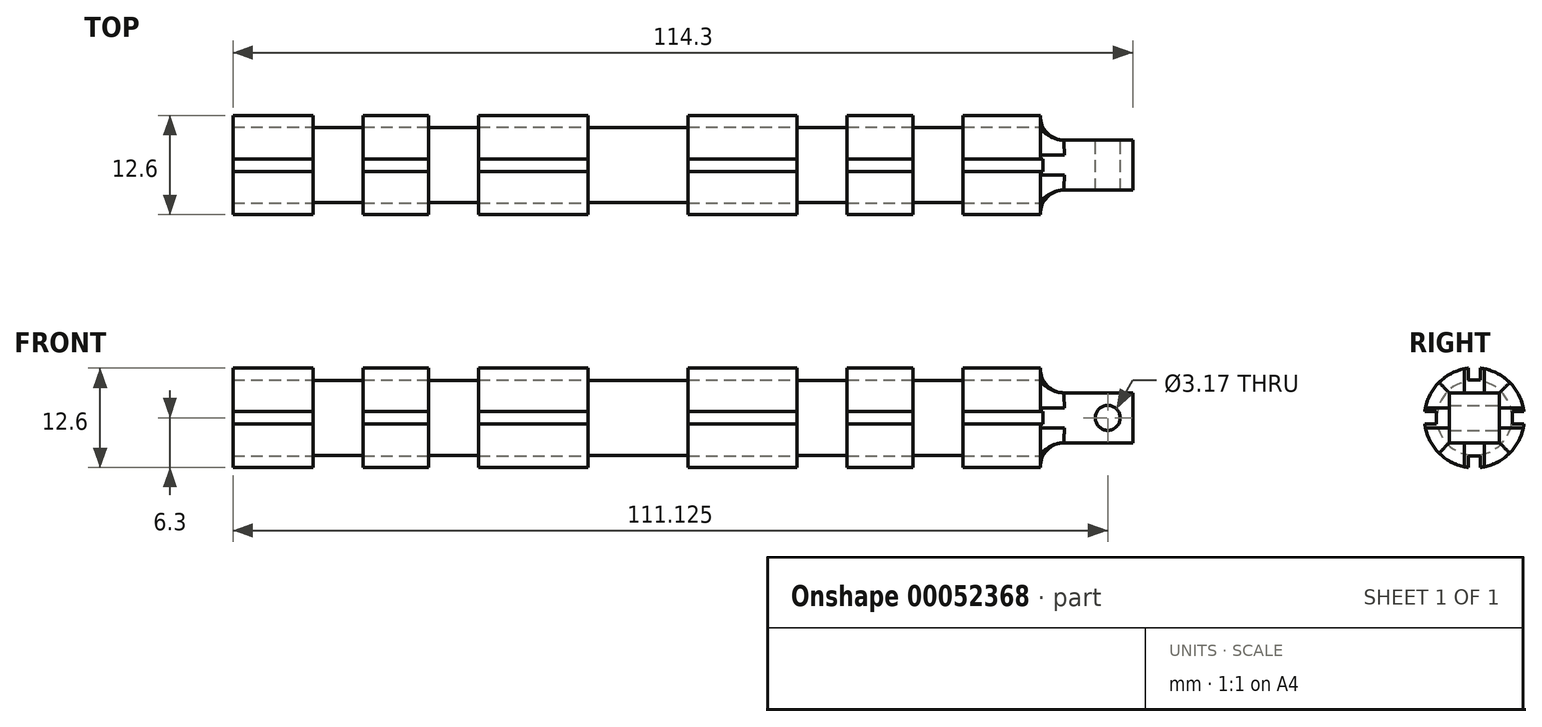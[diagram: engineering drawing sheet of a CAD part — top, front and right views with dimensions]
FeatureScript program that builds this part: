
annotation { "Feature Type Name" : "Feature", "Feature Type Description" : "" }
export const myFeature = defineFeature(function(context is Context, id is Id, definition is map)
    precondition{}
    {
        {
            var Q0;
            Q0=qCreatedBy(makeId("Front.planeOp"),FACE);
            var sketch = newSketch(context, id + "F0", { "sketchPlane" : qUnion([Q0])});
            skLineSegment(sketch, "E0", {"start": v(-57.15, 0) * mm, "end": v(57.15, 0) * mm});
            skLineSegment(sketch, "E1", {"start": v(57.15, 0) * mm, "end": v(57.15, 4.76) * mm});
            skLineSegment(sketch, "E2", {"start": v(45.4, 6.35) * mm, "end": v(35.56, 6.35) * mm});
            skLineSegment(sketch, "E3", {"start": v(35.56, 6.35) * mm, "end": v(35.56, 4.76) * mm});
            skLineSegment(sketch, "E4", {"start": v(35.56, 4.76) * mm, "end": v(29.21, 4.76) * mm});
            skLineSegment(sketch, "E5", {"start": v(29.21, 4.76) * mm, "end": v(29.21, 6.35) * mm});
            skLineSegment(sketch, "E6", {"start": v(29.21, 6.35) * mm, "end": v(20.88, 6.35) * mm});
            skLineSegment(sketch, "E7", {"start": v(20.88, 6.35) * mm, "end": v(20.88, 4.76) * mm});
            skLineSegment(sketch, "E8", {"start": v(20.88, 4.76) * mm, "end": v(14.53, 4.76) * mm});
            skLineSegment(sketch, "E9", {"start": v(14.53, 4.76) * mm, "end": v(14.53, 6.35) * mm});
            skLineSegment(sketch, "E10", {"start": v(14.53, 6.35) * mm, "end": v(0.63, 6.35) * mm});
            skLineSegment(sketch, "E11", {"start": v(0.63, 6.35) * mm, "end": v(0.63, 4.76) * mm});
            skLineSegment(sketch, "E12", {"start": v(0.63, 4.76) * mm, "end": v(-12.07, 4.76) * mm});
            skLineSegment(sketch, "E13", {"start": v(-12.07, 4.76) * mm, "end": v(-12.07, 6.35) * mm});
            skLineSegment(sketch, "E14", {"start": v(-12.07, 6.35) * mm, "end": v(-25.96, 6.35) * mm});
            skLineSegment(sketch, "E15", {"start": v(-25.96, 6.35) * mm, "end": v(-25.96, 4.76) * mm});
            skLineSegment(sketch, "E16", {"start": v(-25.96, 4.76) * mm, "end": v(-32.3, 4.76) * mm});
            skLineSegment(sketch, "E17", {"start": v(-32.3, 4.76) * mm, "end": v(-32.3, 6.35) * mm});
            skLineSegment(sketch, "E18", {"start": v(-32.3, 6.35) * mm, "end": v(-40.64, 6.35) * mm});
            skLineSegment(sketch, "E19", {"start": v(-40.64, 6.35) * mm, "end": v(-40.64, 4.76) * mm});
            skLineSegment(sketch, "E20", {"start": v(-40.64, 4.76) * mm, "end": v(-47, 4.76) * mm});
            skLineSegment(sketch, "E21", {"start": v(-47, 4.76) * mm, "end": v(-47, 6.35) * mm});
            skLineSegment(sketch, "E22", {"start": v(-47, 6.35) * mm, "end": v(-57.15, 6.35) * mm});
            skLineSegment(sketch, "E23", {"start": v(-57.15, 6.35) * mm, "end": v(-57.15, 0) * mm});
            skLineSegment(sketch, "E24", {"start": v(45.4, 6.35) * mm, "end": v(45.4, 4.76) * mm});
            skLineSegment(sketch, "E25", {"start": v(57.15, 4.76) * mm, "end": v(45.4, 4.76) * mm});
            skSolve(sketch);
        }
        {
            var Q0;
            Q0 = qSketchRegion(id + "F0", true);
            var Q1;
            Q1=sQuery(id+"F0.wireOp",EDGE,"E0");
            revolve(context, id + "F1", {"entities" : qUnion([Q0]), "axis" : qUnion([Q1]), "revolveType" : RevolveType.FULL});
        }
        {
            var Q0;
            Q0=makeQuery(id+"F1.opRevolve","SWEPT_FACE",FACE,{"disambiguationData":[OSD([sQuery(id+"F0.wireOp",EDGE,"E1")])]});
            var sketch = newSketch(context, id + "F2", { "sketchPlane" : qUnion([Q0])});
            skCircle(sketch, "E26.0", {"center": v(0, 0) * mm, "radius": 4.76 * mm});
            skLineSegment(sketch, "E27.rect.bottom", {"start": v(-3.17, 3.18) * mm, "end": v(3.18, 3.18) * mm});
            skLineSegment(sketch, "E27.rect.top", {"start": v(-3.18, -3.18) * mm, "end": v(3.17, -3.18) * mm});
            skLineSegment(sketch, "E27.rect.left", {"start": v(-3.17, 3.18) * mm, "end": v(-3.18, -3.17) * mm});
            skLineSegment(sketch, "E27.rect.right", {"start": v(3.18, 3.18) * mm, "end": v(3.17, -3.18) * mm});
            skSolve(sketch);
        }
        {
            var Q0;
            Q0 = qSketchRegion(id + "F2", true);
            extrude(context, id + "F3", {"entities" : qUnion([Q0]), "operationType" : NewBodyOperationType.REMOVE, "oppositeDirection" : true, "depth" : 11.75 * mm});
        }
        {
            var Q0;
            Q0=makeQuery(id+"F3.boolean.opBoolean","COPY",FACE,{"derivedFrom":makeQuery(id+"F3.opExtrude","SWEPT_FACE",FACE,{"disambiguationData":[OSD([sQuery(id+"F2.wireOp",EDGE,"E27.rect.left")])]})});
            var sketch = newSketch(context, id + "F4", { "sketchPlane" : qUnion([Q0])});
            skPoint(sketch, "E28", {"position": v(53.98, 0) * mm});
            skSolve(sketch);
        }
        {
            var Q0;
            Q0=sQuery(id+"F4.wireOp",VERTEX,"E28");
            var Q1;
            Q1=makeQuery(id+"F1.opRevolve","SWEPT_BODY",BODY,{"disambiguationData":[OSD([sQuery(id+"F0.wireOp",EDGE,"E0"),sQuery(id+"F0.wireOp",EDGE,"E1"),sQuery(id+"F0.wireOp",EDGE,"E2"),sQuery(id+"F0.wireOp",EDGE,"E3"),sQuery(id+"F0.wireOp",EDGE,"E4"),sQuery(id+"F0.wireOp",EDGE,"E5"),sQuery(id+"F0.wireOp",EDGE,"E6"),sQuery(id+"F0.wireOp",EDGE,"E7"),sQuery(id+"F0.wireOp",EDGE,"E8"),sQuery(id+"F0.wireOp",EDGE,"E9"),sQuery(id+"F0.wireOp",EDGE,"E10"),sQuery(id+"F0.wireOp",EDGE,"E11"),sQuery(id+"F0.wireOp",EDGE,"E12"),sQuery(id+"F0.wireOp",EDGE,"E13"),sQuery(id+"F0.wireOp",EDGE,"E14"),sQuery(id+"F0.wireOp",EDGE,"E15"),sQuery(id+"F0.wireOp",EDGE,"E16"),sQuery(id+"F0.wireOp",EDGE,"E17"),sQuery(id+"F0.wireOp",EDGE,"E18"),sQuery(id+"F0.wireOp",EDGE,"E19"),sQuery(id+"F0.wireOp",EDGE,"E20"),sQuery(id+"F0.wireOp",EDGE,"E21"),sQuery(id+"F0.wireOp",EDGE,"E22"),sQuery(id+"F0.wireOp",EDGE,"E23"),sQuery(id+"F0.wireOp",EDGE,"E24"),sQuery(id+"F0.wireOp",EDGE,"E25")])]});
            hole(context, id + "F5", {"style" : HoleStyle.SIMPLE, "holeDiameter" : 3.17 * mm, "endStyle" : HoleEndStyle.THROUGH, "locations" : qUnion([Q0]), "scope" : qUnion([Q1])});
        }
        {
            var Q0;
            Q0=makeQuery(id+"F3.boolean.opBoolean","COPY",EDGE,{"derivedFrom":makeQuery(id+"F3.opExtrude","CAP_EDGE",EDGE,{"disambiguationData":[OSD([sQuery(id+"F2.wireOp",EDGE,"E27.rect.bottom")])],"isStart":false})});
            var Q1;
            Q1=makeQuery(id+"F3.boolean.opBoolean","COPY",EDGE,{"derivedFrom":makeQuery(id+"F3.opExtrude","CAP_EDGE",EDGE,{"disambiguationData":[OSD([sQuery(id+"F2.wireOp",EDGE,"E27.rect.left")])],"isStart":false})});
            var Q2;
            Q2=makeQuery(id+"F3.boolean.opBoolean","COPY",EDGE,{"derivedFrom":makeQuery(id+"F3.opExtrude","CAP_EDGE",EDGE,{"disambiguationData":[OSD([sQuery(id+"F2.wireOp",EDGE,"E27.rect.top")])],"isStart":false})});
            var Q3;
            Q3=makeQuery(id+"F3.boolean.opBoolean","COPY",EDGE,{"derivedFrom":makeQuery(id+"F3.opExtrude","CAP_EDGE",EDGE,{"disambiguationData":[OSD([sQuery(id+"F2.wireOp",EDGE,"E27.rect.right")])],"isStart":false})});
            fillet(context, id + "F6", {"entities" : qUnion([Q0, Q1, Q2, Q3]), "radius" : 3.05 * mm, "tangentPropagation" : true, "allowEdgeOverflow" : false});
        }
        {
            var Q0;
            Q0=qCreatedBy(makeId("Right.planeOp"),FACE);
            var sketch = newSketch(context, id + "F7", { "sketchPlane" : qUnion([Q0])});
            skLineSegment(sketch, "E29.rect.bottom", {"start": v(-0.79, 6.35) * mm, "end": v(0.79, 6.35) * mm});
            skLineSegment(sketch, "E29.rect.top", {"start": v(-0.79, 4.83) * mm, "end": v(0.79, 4.83) * mm});
            skLineSegment(sketch, "E29.rect.left", {"start": v(-0.79, 6.35) * mm, "end": v(-0.79, 4.83) * mm});
            skLineSegment(sketch, "E29.rect.right", {"start": v(0.79, 6.35) * mm, "end": v(0.79, 4.83) * mm});
            skPoint(sketch, "E29.rect.middle", {"position": v(0, 5.59) * mm});
            skLineSegment(sketch, "E30.rect.bottom", {"start": v(-4.83, -0.79) * mm, "end": v(-6.35, -0.79) * mm});
            skLineSegment(sketch, "E30.rect.top", {"start": v(-4.83, 0.79) * mm, "end": v(-6.35, 0.79) * mm});
            skLineSegment(sketch, "E30.rect.left", {"start": v(-4.83, -0.79) * mm, "end": v(-4.83, 0.79) * mm});
            skLineSegment(sketch, "E30.rect.right", {"start": v(-6.35, -0.79) * mm, "end": v(-6.35, 0.79) * mm});
            skPoint(sketch, "E30.rect.middle", {"position": v(-5.59, 0) * mm});
            skLineSegment(sketch, "E31.rect.bottom", {"start": v(6.35, -0.79) * mm, "end": v(4.83, -0.79) * mm});
            skLineSegment(sketch, "E31.rect.top", {"start": v(6.35, 0.79) * mm, "end": v(4.83, 0.79) * mm});
            skLineSegment(sketch, "E31.rect.left", {"start": v(6.35, -0.79) * mm, "end": v(6.35, 0.79) * mm});
            skLineSegment(sketch, "E31.rect.right", {"start": v(4.83, -0.79) * mm, "end": v(4.83, 0.79) * mm});
            skPoint(sketch, "E31.rect.middle", {"position": v(5.59, 0) * mm});
            skLineSegment(sketch, "E32.rect.bottom", {"start": v(0.79, -6.35) * mm, "end": v(-0.79, -6.35) * mm});
            skLineSegment(sketch, "E32.rect.top", {"start": v(0.79, -4.83) * mm, "end": v(-0.79, -4.83) * mm});
            skLineSegment(sketch, "E32.rect.left", {"start": v(0.79, -6.35) * mm, "end": v(0.79, -4.83) * mm});
            skLineSegment(sketch, "E32.rect.right", {"start": v(-0.79, -6.35) * mm, "end": v(-0.79, -4.83) * mm});
            skPoint(sketch, "E32.rect.middle", {"position": v(0, -5.59) * mm});
            skSolve(sketch);
        }
        {
            var Q0;
            Q0 = qSketchRegion(id + "F7", true);
            extrude(context, id + "F8", {"entities" : qUnion([Q0]), "operationType" : NewBodyOperationType.REMOVE, "oppositeDirection" : true, "depth" : 127 * mm, "symmetric" : true});
        }
    });
